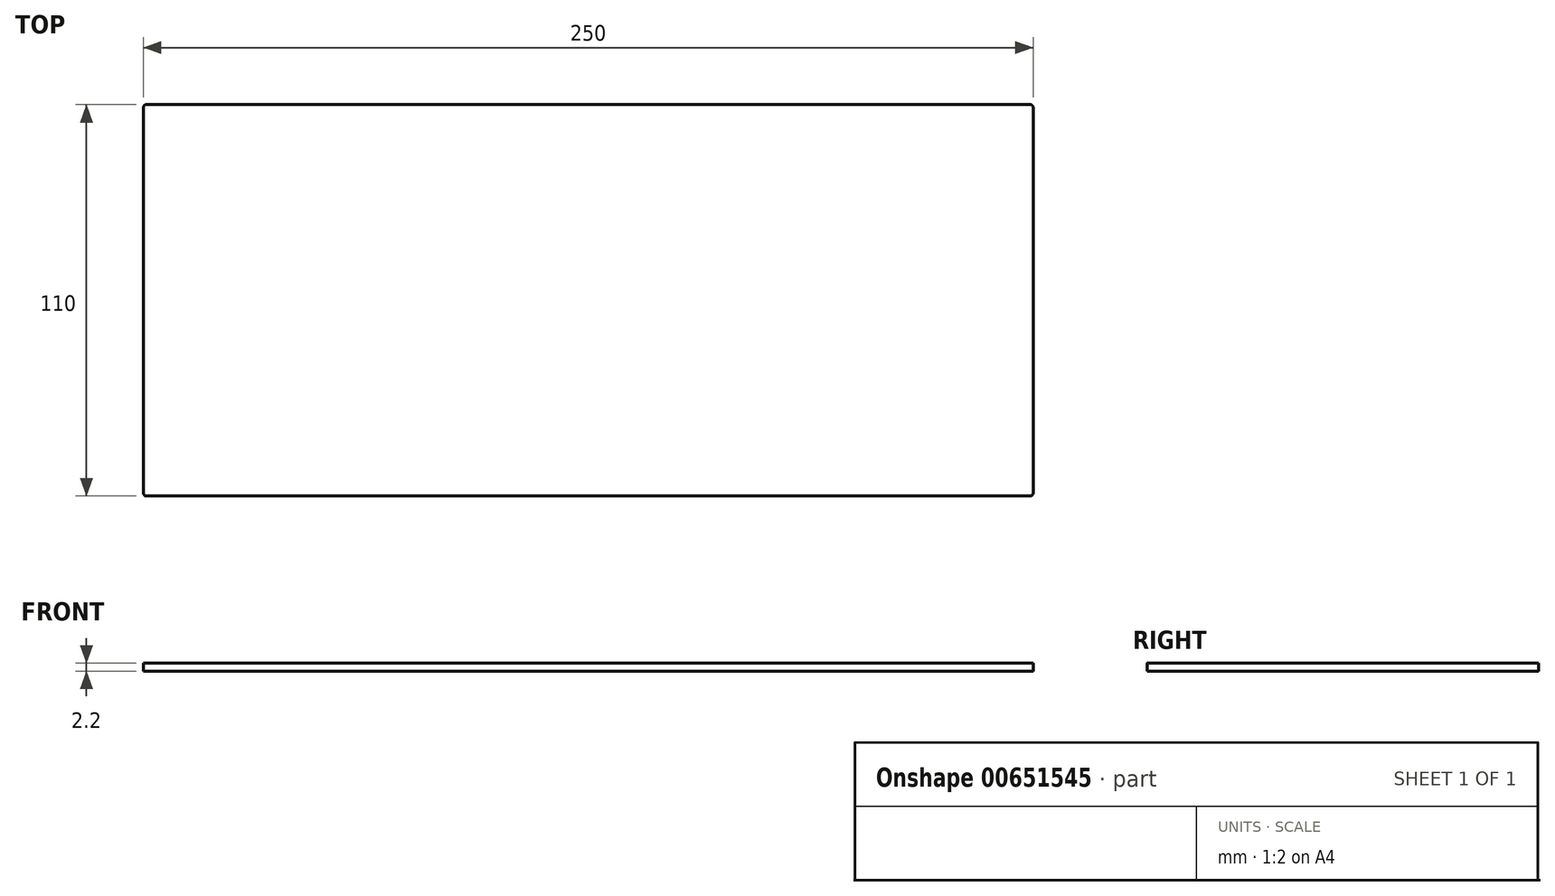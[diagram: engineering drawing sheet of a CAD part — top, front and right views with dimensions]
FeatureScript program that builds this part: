
annotation { "Feature Type Name" : "Feature", "Feature Type Description" : "" }
export const myFeature = defineFeature(function(context is Context, id is Id, definition is map)
    precondition{}
    {
        {
            var Q0;
            Q0=qCreatedBy(makeId("Top.planeOp"),FACE);
            var sketch = newSketch(context, id + "F0", { "sketchPlane" : qUnion([Q0])});
            skLineSegment(sketch, "E0.bottom", {"start": v(-125, 55) * mm, "end": v(125, 55) * mm});
            skLineSegment(sketch, "E0.top", {"start": v(-125, -55) * mm, "end": v(125, -55) * mm});
            skLineSegment(sketch, "E0.left", {"start": v(-125, 55) * mm, "end": v(-125, -55) * mm});
            skLineSegment(sketch, "E0.right", {"start": v(125, 55) * mm, "end": v(125, -55) * mm});
            skPoint(sketch, "E0.middle", {"position": v(0, 0) * mm});
            skSolve(sketch);
        }
        {
            var Q0;
            Q0=makeQuery(id+"F0.imprint","IMPRINT",FACE,{"disambiguationData":[TD([[makeQuery(id+"F0.imprint","IMPRINT",EDGE,{"derivedFrom":sQuery(id+"F0.wireOp",EDGE,"E0.bottom")}),-1.0]])]});
            extrude(context, id + "F1", {"entities" : qUnion([Q0]), "depth" : 2.2 * mm, "offsetDistance" : 25 * mm});
        }
        {
            var Q0;
            Q0=makeQuery(id+"F1.opExtrude","SWEPT_EDGE",EDGE,{"disambiguationData":[OSD([sQuery(id+"F0.wireOp",EDGE,"E0.top"),sQuery(id+"F0.wireOp",EDGE,"E0.left")])]});
            var Q1;
            Q1=makeQuery(id+"F1.opExtrude","SWEPT_EDGE",EDGE,{"disambiguationData":[OSD([sQuery(id+"F0.wireOp",EDGE,"E0.top"),sQuery(id+"F0.wireOp",EDGE,"E0.right")])]});
            var Q2;
            Q2=makeQuery(id+"F1.opExtrude","SWEPT_EDGE",EDGE,{"disambiguationData":[OSD([sQuery(id+"F0.wireOp",EDGE,"E0.bottom"),sQuery(id+"F0.wireOp",EDGE,"E0.right")])]});
            var Q3;
            Q3=makeQuery(id+"F1.opExtrude","SWEPT_EDGE",EDGE,{"disambiguationData":[OSD([sQuery(id+"F0.wireOp",EDGE,"E0.bottom"),sQuery(id+"F0.wireOp",EDGE,"E0.left")])]});
            fillet(context, id + "F2", {"entities" : qUnion([Q0, Q1, Q2, Q3]), "radius" : 0.8 * mm, "tangentPropagation" : true, "allowEdgeOverflow" : false});
        }
    });
